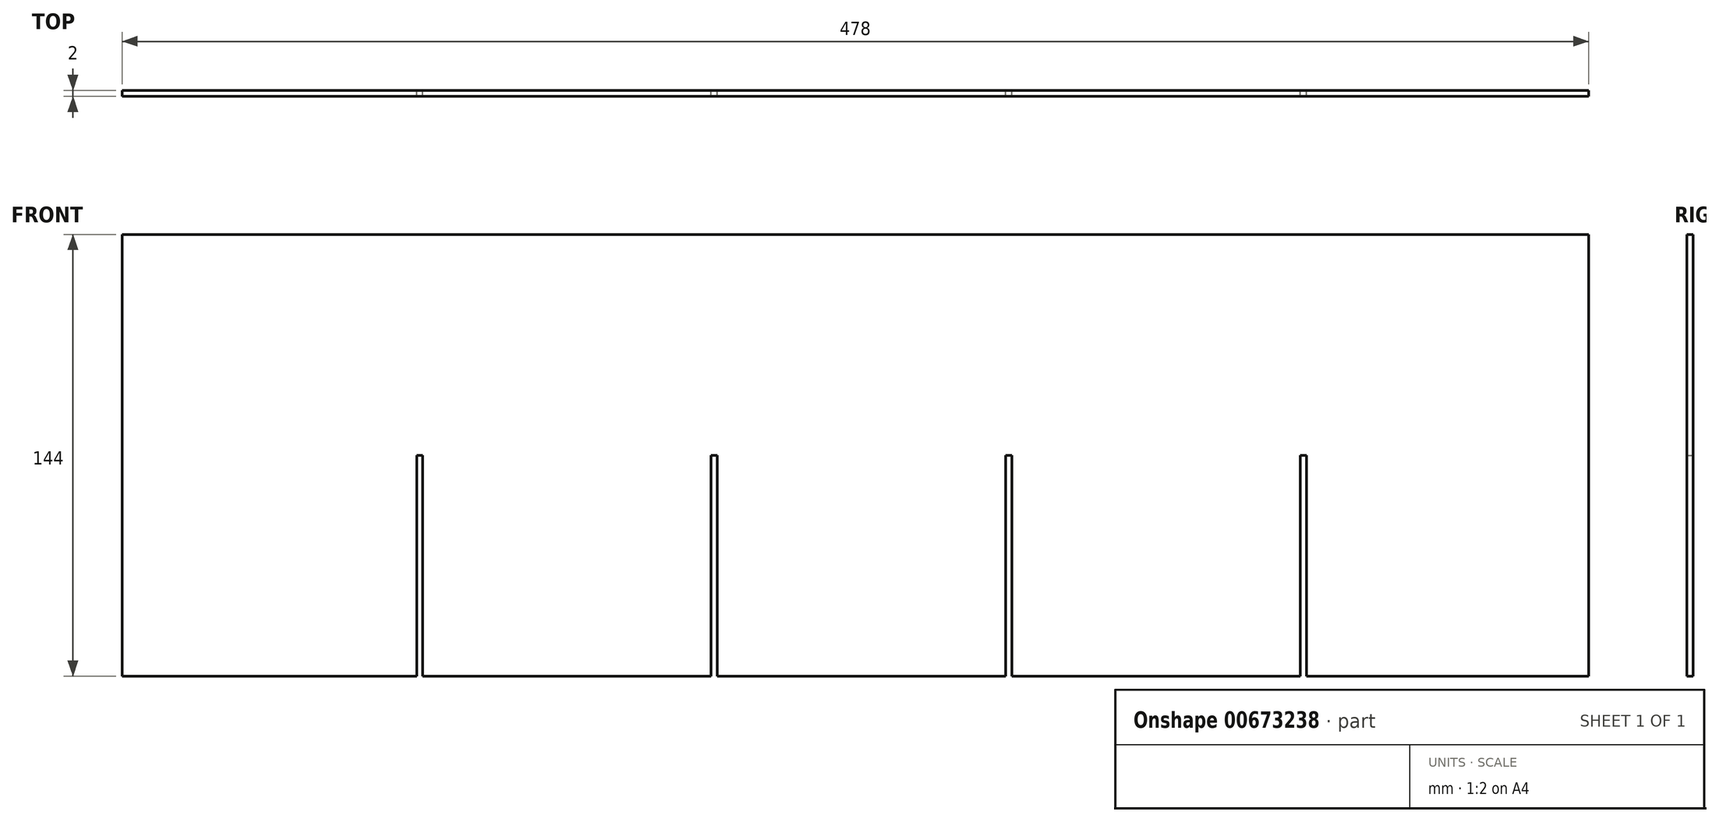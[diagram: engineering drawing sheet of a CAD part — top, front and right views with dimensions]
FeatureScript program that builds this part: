
annotation { "Feature Type Name" : "Feature", "Feature Type Description" : "" }
export const myFeature = defineFeature(function(context is Context, id is Id, definition is map)
    precondition{}
    {
        {
            var Q0;
            Q0=qCreatedBy(makeId("Front.planeOp"),FACE);
            var sketch = newSketch(context, id + "F0", { "sketchPlane" : qUnion([Q0])});
            skLineSegment(sketch, "E0.bottom", {"start": v(-239, -72) * mm, "end": v(-143, -72) * mm});
            skLineSegment(sketch, "E0.top", {"start": v(-239, 72) * mm, "end": v(239, 72) * mm});
            skLineSegment(sketch, "E0.left", {"start": v(-239, -72) * mm, "end": v(-239, 72) * mm});
            skLineSegment(sketch, "E0.right", {"start": v(239, -72) * mm, "end": v(239, 72) * mm});
            skPoint(sketch, "E0.middle", {"position": v(0, 0) * mm});
            skLineSegment(sketch, "E1", {"start": v(-143, -72) * mm, "end": v(-143, 0) * mm});
            skLineSegment(sketch, "E2", {"start": v(-143, 0) * mm, "end": v(-141, 0) * mm});
            skLineSegment(sketch, "E3", {"start": v(-141, 0) * mm, "end": v(-141, -72) * mm});
            skLineSegment(sketch, "E4.trimOffspring", {"start": v(-141, -72) * mm, "end": v(-47, -72) * mm});
            skLineSegment(sketch, "E5.1.0.0", {"start": v(-47, -72) * mm, "end": v(-47, 0) * mm});
            skLineSegment(sketch, "E5.1.0.1", {"start": v(-45, 0) * mm, "end": v(-45, -72) * mm});
            skLineSegment(sketch, "E5.1.0.2", {"start": v(-47, 0) * mm, "end": v(-45, 0) * mm});
            skLineSegment(sketch, "E5.2.0.0", {"start": v(49, -72) * mm, "end": v(49, 0) * mm});
            skLineSegment(sketch, "E5.2.0.1", {"start": v(51, 0) * mm, "end": v(51, -72) * mm});
            skLineSegment(sketch, "E5.2.0.2", {"start": v(49, 0) * mm, "end": v(51, 0) * mm});
            skLineSegment(sketch, "E5.3.0.0", {"start": v(145, -72) * mm, "end": v(145, 0) * mm});
            skLineSegment(sketch, "E5.3.0.1", {"start": v(147, 0) * mm, "end": v(147, -72) * mm});
            skLineSegment(sketch, "E5.3.0.2", {"start": v(145, 0) * mm, "end": v(147, 0) * mm});
            skLineSegment(sketch, "E5.direction1", {"start": v(-143, -72) * mm, "end": v(-47, -72) * mm, "construction": true});
            skLineSegment(sketch, "E6.trimOffspring", {"start": v(147, -72) * mm, "end": v(239, -72) * mm});
            skLineSegment(sketch, "E7.trimOffspring", {"start": v(51, -72) * mm, "end": v(145, -72) * mm});
            skLineSegment(sketch, "E8.trimOffspring", {"start": v(-45, -72) * mm, "end": v(49, -72) * mm});
            skSolve(sketch);
        }
        {
            var Q0;
            Q0=makeQuery(id+"F0.imprint","IMPRINT",FACE,{"disambiguationData":[TD([[makeQuery(id+"F0.imprint","IMPRINT",EDGE,{"derivedFrom":sQuery(id+"F0.wireOp",EDGE,"E0.bottom")}),1.0]])]});
            extrude(context, id + "F1", {"entities" : qUnion([Q0]), "endBound" : BoundingType.SYMMETRIC, "depth" : 2 * mm, "offsetDistance" : 25 * mm});
        }
    });
